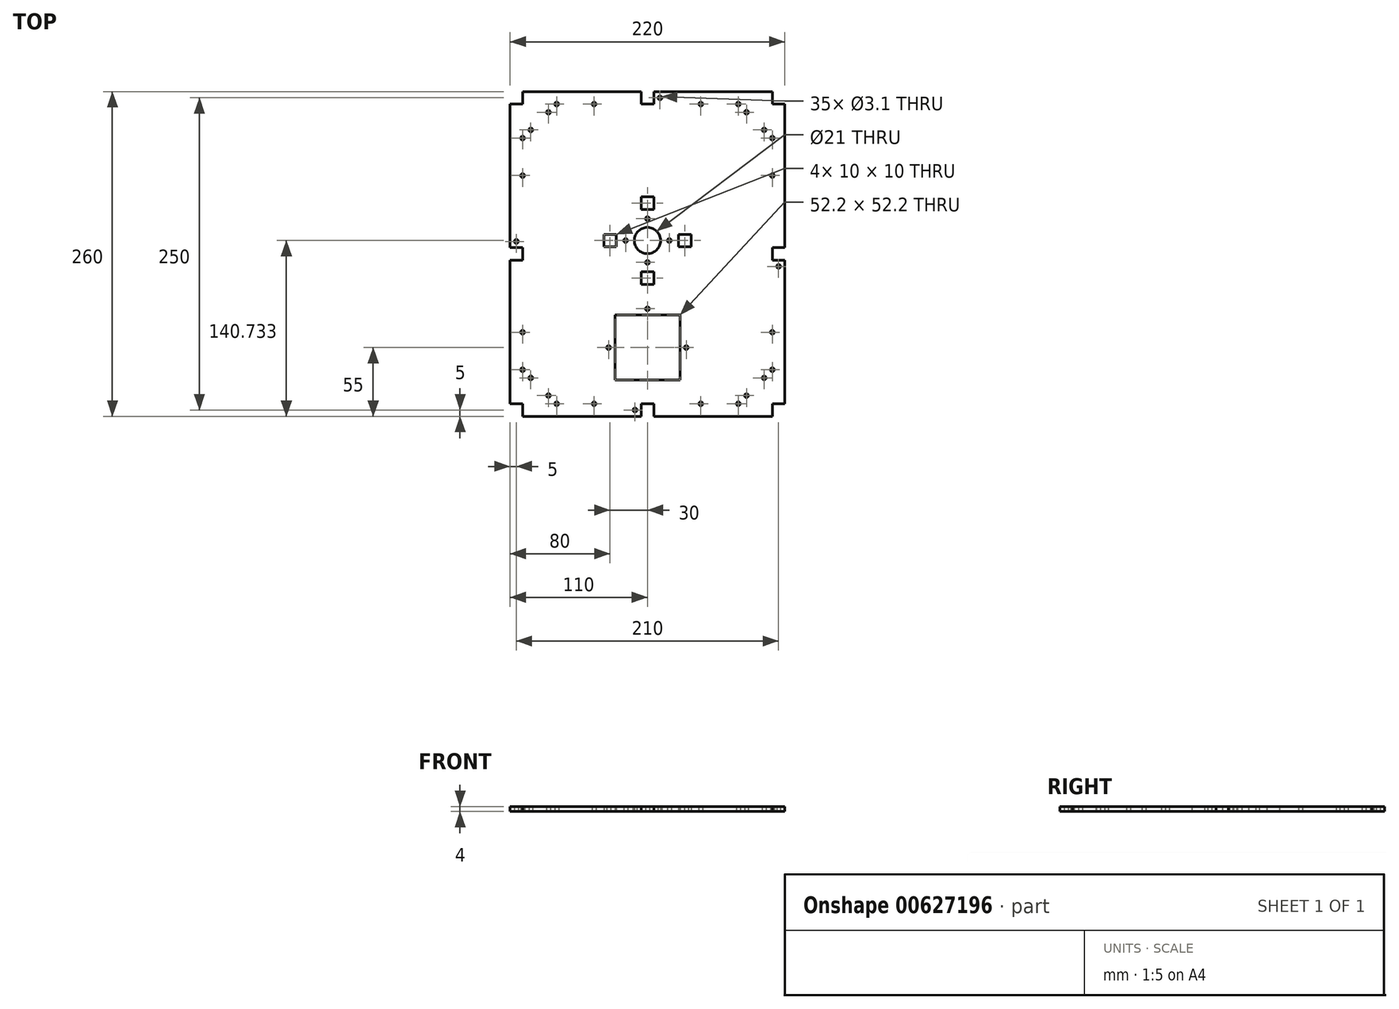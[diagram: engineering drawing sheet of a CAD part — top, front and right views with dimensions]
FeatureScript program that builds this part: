
annotation { "Feature Type Name" : "Feature", "Feature Type Description" : "" }
export const myFeature = defineFeature(function(context is Context, id is Id, definition is map)
    precondition{}
    {
        {
            var Q0;
            Q0=qCreatedBy(makeId("Top.planeOp"),FACE);
            var sketch = newSketch(context, id + "F0", { "sketchPlane" : qUnion([Q0])});
            skLineSegment(sketch, "E0.bottom", {"start": v(0, 0) * mm, "end": v(220, 0) * mm});
            skLineSegment(sketch, "E0.top", {"start": v(0, 260) * mm, "end": v(220, 260) * mm});
            skLineSegment(sketch, "E0.left", {"start": v(0, 0) * mm, "end": v(0, 260) * mm});
            skLineSegment(sketch, "E0.right", {"start": v(220, 0) * mm, "end": v(220, 260) * mm});
            skLineSegment(sketch, "E1.bottom", {"start": v(0, 260) * mm, "end": v(10, 260) * mm});
            skLineSegment(sketch, "E1.top", {"start": v(0, 250) * mm, "end": v(10, 250) * mm});
            skLineSegment(sketch, "E1.left", {"start": v(0, 260) * mm, "end": v(0, 250) * mm});
            skLineSegment(sketch, "E1.right", {"start": v(10, 260) * mm, "end": v(10, 250) * mm});
            skLineSegment(sketch, "E2.bottom", {"start": v(220, 260) * mm, "end": v(210, 260) * mm});
            skLineSegment(sketch, "E2.top", {"start": v(220, 250) * mm, "end": v(210, 250) * mm});
            skLineSegment(sketch, "E2.left", {"start": v(220, 260) * mm, "end": v(220, 250) * mm});
            skLineSegment(sketch, "E2.right", {"start": v(210, 260) * mm, "end": v(210, 250) * mm});
            skLineSegment(sketch, "E3.bottom", {"start": v(220, 0) * mm, "end": v(210, 0) * mm});
            skLineSegment(sketch, "E3.top", {"start": v(220, 10) * mm, "end": v(210, 10) * mm});
            skLineSegment(sketch, "E3.left", {"start": v(220, 0) * mm, "end": v(220, 10) * mm});
            skLineSegment(sketch, "E3.right", {"start": v(210, 0) * mm, "end": v(210, 10) * mm});
            skLineSegment(sketch, "E4.bottom", {"start": v(0, 0) * mm, "end": v(10, 0) * mm});
            skLineSegment(sketch, "E4.top", {"start": v(0, 10) * mm, "end": v(10, 10) * mm});
            skLineSegment(sketch, "E4.left", {"start": v(0, 0) * mm, "end": v(0, 10) * mm});
            skLineSegment(sketch, "E4.right", {"start": v(10, 0) * mm, "end": v(10, 10) * mm});
            skCircle(sketch, "E5", {"center": v(10, 222.73) * mm, "radius": 1.55 * mm});
            skCircle(sketch, "E6", {"center": v(10, 192.73) * mm, "radius": 1.55 * mm});
            skLineSegment(sketch, "E7", {"start": v(0, 260) * mm, "end": v(10, 250) * mm, "construction": true});
            skCircle(sketch, "E8.MirrorC", {"center": v(37.26, 250) * mm, "radius": 1.55 * mm});
            skCircle(sketch, "E9.MirrorC", {"center": v(67.26, 250) * mm, "radius": 1.55 * mm});
            skLineSegment(sketch, "E10", {"start": v(110, 329.94) * mm, "end": v(110, -90.06) * mm, "construction": true});
            skLineSegment(sketch, "E11", {"start": v(-110.2, 130) * mm, "end": v(289.8, 130) * mm, "construction": true});
            skLineSegment(sketch, "E12", {"start": v(165, 329.94) * mm, "end": v(165, -90.06) * mm, "construction": true});
            skLineSegment(sketch, "E13", {"start": v(55, 329.94) * mm, "end": v(55, -90.06) * mm, "construction": true});
            skCircle(sketch, "E14.MirrorC", {"center": v(152.73, 250) * mm, "radius": 1.55 * mm});
            skCircle(sketch, "E15.MirrorC", {"center": v(182.73, 250) * mm, "radius": 1.55 * mm});
            skCircle(sketch, "E16.MirrorC", {"center": v(210, 222.74) * mm, "radius": 1.55 * mm});
            skCircle(sketch, "E17.MirrorC", {"center": v(210, 192.73) * mm, "radius": 1.55 * mm});
            skCircle(sketch, "E18.MirrorC", {"center": v(10, 67.27) * mm, "radius": 1.55 * mm});
            skCircle(sketch, "E19.MirrorC", {"center": v(10, 37.27) * mm, "radius": 1.55 * mm});
            skCircle(sketch, "E20.MirrorC", {"center": v(37.26, 10) * mm, "radius": 1.55 * mm});
            skCircle(sketch, "E21.MirrorC", {"center": v(67.26, 10) * mm, "radius": 1.55 * mm});
            skCircle(sketch, "E22.MirrorC", {"center": v(152.73, 10) * mm, "radius": 1.55 * mm});
            skCircle(sketch, "E23.MirrorC", {"center": v(182.73, 10) * mm, "radius": 1.55 * mm});
            skCircle(sketch, "E24.MirrorC", {"center": v(210, 37.26) * mm, "radius": 1.55 * mm});
            skCircle(sketch, "E25.MirrorC", {"center": v(210, 67.27) * mm, "radius": 1.55 * mm});
            skLineSegment(sketch, "E26.bottom", {"start": v(0, 135) * mm, "end": v(10, 135) * mm});
            skLineSegment(sketch, "E26.top", {"start": v(0, 125) * mm, "end": v(10, 125) * mm});
            skLineSegment(sketch, "E26.left", {"start": v(0, 135) * mm, "end": v(0, 125) * mm});
            skLineSegment(sketch, "E26.right", {"start": v(10, 135) * mm, "end": v(10, 125) * mm});
            skLineSegment(sketch, "E27.MirrorCS", {"start": v(220, 135) * mm, "end": v(210, 135) * mm});
            skLineSegment(sketch, "E28.MirrorCS", {"start": v(220, 135) * mm, "end": v(220, 125) * mm});
            skLineSegment(sketch, "E29.MirrorCS", {"start": v(220, 125) * mm, "end": v(210, 125) * mm});
            skLineSegment(sketch, "E30.MirrorCS", {"start": v(210, 135) * mm, "end": v(210, 125) * mm});
            skLineSegment(sketch, "E31.bottom", {"start": v(136.1, 28.9) * mm, "end": v(83.9, 28.9) * mm});
            skLineSegment(sketch, "E31.top", {"start": v(136.1, 81.1) * mm, "end": v(83.9, 81.1) * mm});
            skLineSegment(sketch, "E31.left", {"start": v(136.1, 28.9) * mm, "end": v(136.1, 81.1) * mm});
            skLineSegment(sketch, "E31.right", {"start": v(83.9, 28.9) * mm, "end": v(83.9, 81.1) * mm});
            skPoint(sketch, "E31.middle", {"position": v(110, 55) * mm});
            skCircle(sketch, "E32", {"center": v(141.1, 55) * mm, "radius": 1.55 * mm});
            skCircle(sketch, "E33", {"center": v(110, 86.1) * mm, "radius": 1.55 * mm});
            skCircle(sketch, "E34.MirrorC", {"center": v(78.9, 55) * mm, "radius": 1.55 * mm});
            skLineSegment(sketch, "E35.bottom", {"start": v(115, 250) * mm, "end": v(105, 250) * mm});
            skLineSegment(sketch, "E35.top", {"start": v(115, 260) * mm, "end": v(105, 260) * mm});
            skLineSegment(sketch, "E35.left", {"start": v(115, 250) * mm, "end": v(115, 260) * mm});
            skLineSegment(sketch, "E35.right", {"start": v(105, 250) * mm, "end": v(105, 260) * mm});
            skPoint(sketch, "E35.middle", {"position": v(110, 255) * mm});
            skLineSegment(sketch, "E36.MirrorCS", {"start": v(105, 10) * mm, "end": v(105, 0) * mm});
            skLineSegment(sketch, "E37.MirrorCS", {"start": v(115, 0) * mm, "end": v(105, 0) * mm});
            skLineSegment(sketch, "E38.MirrorCS", {"start": v(115, 10) * mm, "end": v(115, 0) * mm});
            skLineSegment(sketch, "E39.MirrorCS", {"start": v(115, 10) * mm, "end": v(105, 10) * mm});
            skCircle(sketch, "E40", {"center": v(120, 255) * mm, "radius": 1.55 * mm});
            skPoint(sketch, "E40.centerSnap0", {"position": v(115, 255) * mm});
            skPoint(sketch, "E40.perimeterSnap0", {"position": v(115, 255) * mm});
            skCircle(sketch, "E41", {"center": v(215, 120) * mm, "radius": 1.55 * mm});
            skPoint(sketch, "E41.centerSnap0", {"position": v(215, 125) * mm});
            skPoint(sketch, "E41.perimeterSnap0", {"position": v(215, 125) * mm});
            skCircle(sketch, "E42", {"center": v(100, 5) * mm, "radius": 1.55 * mm});
            skPoint(sketch, "E42.centerSnap0", {"position": v(105, 5) * mm});
            skCircle(sketch, "E43", {"center": v(5, 140) * mm, "radius": 1.55 * mm});
            skPoint(sketch, "E43.centerSnap0", {"position": v(5, 135) * mm});
            skCircle(sketch, "E44", {"center": v(110, 140.73) * mm, "radius": 10.5 * mm});
            skCircle(sketch, "E45", {"center": v(127.5, 140.73) * mm, "radius": 1.55 * mm});
            skCircle(sketch, "E46", {"center": v(92.5, 140.73) * mm, "radius": 1.55 * mm});
            skCircle(sketch, "E47", {"center": v(110, 158.23) * mm, "radius": 1.55 * mm});
            skCircle(sketch, "E48", {"center": v(110, 123.23) * mm, "radius": 1.55 * mm});
            skLineSegment(sketch, "E49.bottom", {"start": v(115, 165.73) * mm, "end": v(105, 165.73) * mm});
            skLineSegment(sketch, "E49.top", {"start": v(115, 175.73) * mm, "end": v(105, 175.73) * mm});
            skLineSegment(sketch, "E49.left", {"start": v(115, 165.73) * mm, "end": v(115, 175.73) * mm});
            skLineSegment(sketch, "E49.right", {"start": v(105, 165.73) * mm, "end": v(105, 175.73) * mm});
            skPoint(sketch, "E49.middle", {"position": v(110, 170.73) * mm});
            skLineSegment(sketch, "E50.bottom", {"start": v(145, 135.73) * mm, "end": v(135, 135.73) * mm});
            skLineSegment(sketch, "E50.top", {"start": v(145, 145.73) * mm, "end": v(135, 145.73) * mm});
            skLineSegment(sketch, "E50.left", {"start": v(145, 135.73) * mm, "end": v(145, 145.73) * mm});
            skLineSegment(sketch, "E50.right", {"start": v(135, 135.73) * mm, "end": v(135, 145.73) * mm});
            skPoint(sketch, "E50.middle", {"position": v(140, 140.73) * mm});
            skLineSegment(sketch, "E51.bottom", {"start": v(75, 145.73) * mm, "end": v(85, 145.73) * mm});
            skLineSegment(sketch, "E51.top", {"start": v(75, 135.73) * mm, "end": v(85, 135.73) * mm});
            skLineSegment(sketch, "E51.left", {"start": v(75, 145.73) * mm, "end": v(75, 135.73) * mm});
            skLineSegment(sketch, "E51.right", {"start": v(85, 145.73) * mm, "end": v(85, 135.73) * mm});
            skPoint(sketch, "E51.middle", {"position": v(80, 140.73) * mm});
            skLineSegment(sketch, "E52.bottom", {"start": v(115, 105.73) * mm, "end": v(105, 105.73) * mm});
            skLineSegment(sketch, "E52.top", {"start": v(115, 115.73) * mm, "end": v(105, 115.73) * mm});
            skLineSegment(sketch, "E52.left", {"start": v(115, 105.73) * mm, "end": v(115, 115.73) * mm});
            skLineSegment(sketch, "E52.right", {"start": v(105, 105.73) * mm, "end": v(105, 115.73) * mm});
            skPoint(sketch, "E52.middle", {"position": v(110, 110.73) * mm});
            skLineSegment(sketch, "E53", {"start": v(10, 222.73) * mm, "end": v(37.26, 250) * mm, "construction": true});
            skCircle(sketch, "E54", {"center": v(16.56, 229.3) * mm, "radius": 1.55 * mm});
            skCircle(sketch, "E55", {"center": v(30.7, 243.44) * mm, "radius": 1.55 * mm});
            skLineSegment(sketch, "E56.MirrorCS", {"start": v(10, 37.27) * mm, "end": v(37.26, 10) * mm, "construction": true});
            skCircle(sketch, "E57.MirrorC", {"center": v(203.44, 229.3) * mm, "radius": 1.55 * mm});
            skLineSegment(sketch, "E58.MirrorCS", {"start": v(210, 222.73) * mm, "end": v(182.73, 250) * mm, "construction": true});
            skCircle(sketch, "E59.MirrorC", {"center": v(189.3, 243.44) * mm, "radius": 1.55 * mm});
            skCircle(sketch, "E60.MirrorC", {"center": v(203.44, 30.7) * mm, "radius": 1.55 * mm});
            skLineSegment(sketch, "E61.MirrorCS", {"start": v(210, 37.27) * mm, "end": v(182.73, 10) * mm, "construction": true});
            skCircle(sketch, "E62.MirrorC", {"center": v(189.3, 16.56) * mm, "radius": 1.55 * mm});
            skCircle(sketch, "E63.MirrorC", {"center": v(16.56, 30.7) * mm, "radius": 1.55 * mm});
            skCircle(sketch, "E64.MirrorC", {"center": v(30.7, 16.56) * mm, "radius": 1.55 * mm});
            skSolve(sketch);
        }
        {
            var Q0;
            {var subQ4=sQuery(id+"F0.wireOp",EDGE,"E1.top");Q0=makeQuery(id+"F0.imprint","IMPRINT",FACE,{"disambiguationData":[TD([[makeQuery(id+"F0.imprint","IMPRINT",EDGE,{"derivedFrom":subQ4}),-1.0]])]});}
            extrude(context, id + "F1", {"entities" : qUnion([Q0]), "depth" : 4 * mm, "offsetDistance" : 25 * mm});
        }
    });
